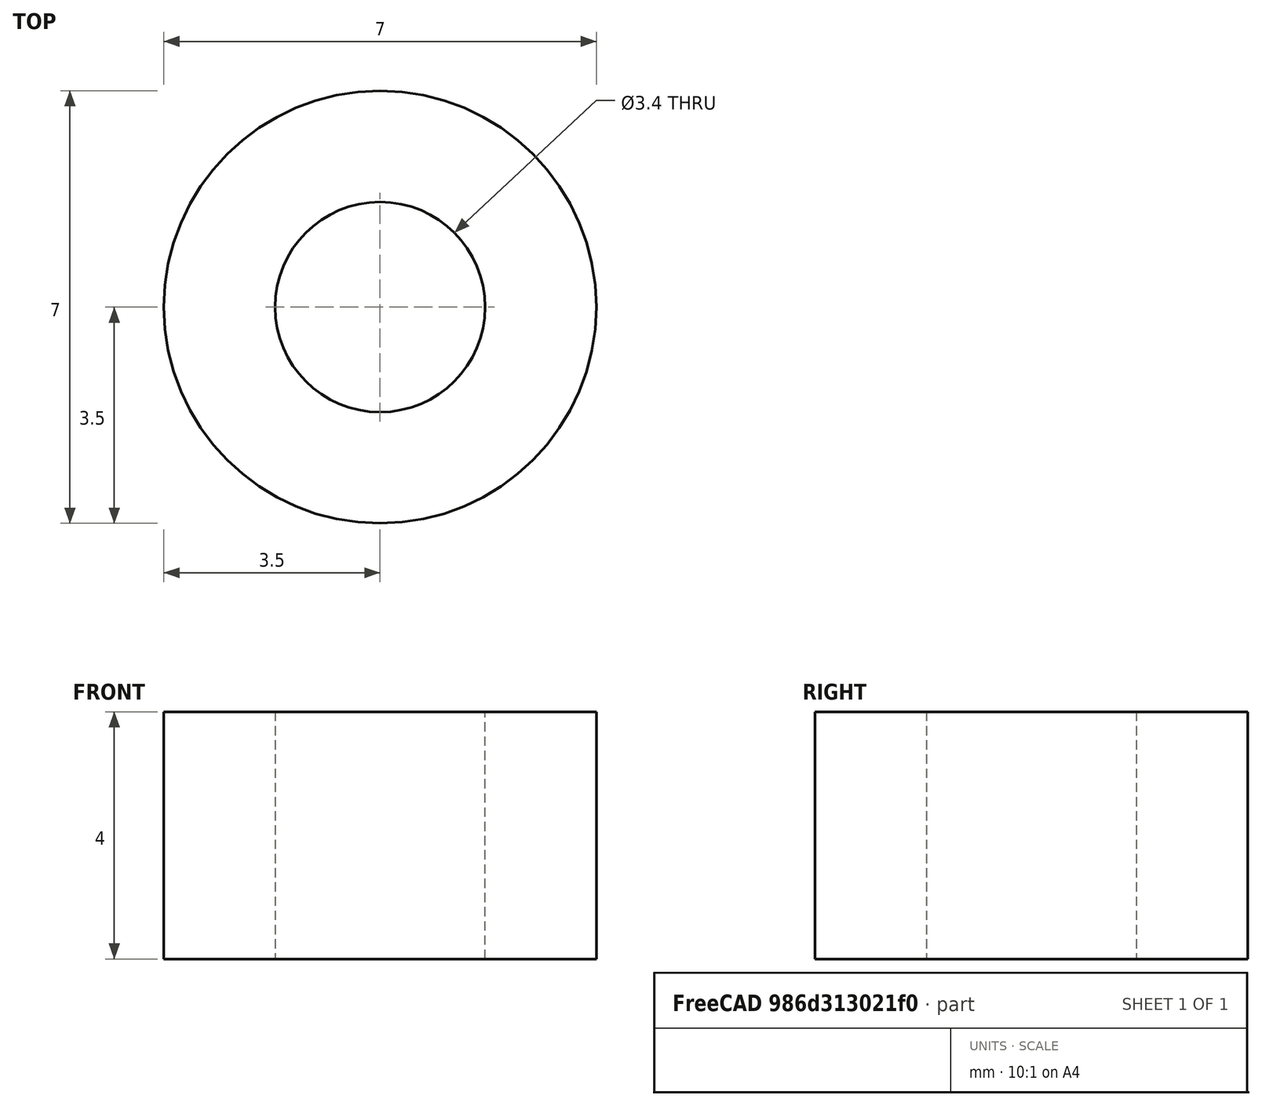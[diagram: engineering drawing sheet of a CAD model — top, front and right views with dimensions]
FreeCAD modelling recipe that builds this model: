
FCSTD DOCUMENT  (FreeCAD 0.19R23578 (Git))
Label: m3_spacer
License: All rights reserved
LicenseURL: http://en.wikipedia.org/wiki/All_rights_reserved
objects: Sketcher::SketchObject×1, PartDesign::Pad×1, PartDesign::Body×1, Mesh::Feature×1
note: 4 computed .brp shape members not serialized (recipe doc carries the construction recipe); baked Part::Feature solids carry a one-line shape summary decoded from their .brp

FEATURE [Sketcher::SketchObject] Sketch
  MapMode = 5
  Support = -> [XY_Plane]
  sketch-geometry (2):
    g0: Circle CenterX=0 CenterY=0 CenterZ=0 NormalX=0 NormalY=0 NormalZ=1 AngleXU=0 Radius=1.7
    g1: Circle CenterX=0 CenterY=0 CenterZ=0 NormalX=0 NormalY=0 NormalZ=1 AngleXU=0 Radius=3.5
  constraints (4):
    c: Coincident(g0,g-1)
    c: Coincident(g1,g0)
    c: Diameter(g0) = 3.4
    c: Diameter(g1) = 7
FEATURE [PartDesign::Pad] Pad
  Direction = (1,1,1)
  Length = 4
  Length2 = 100
  Profile = -> Sketch
  Type = 0
FEATURE [PartDesign::Body] Body
  Group = -> [Sketch,Pad]
  Origin = -> Origin
  Tip = -> Pad
FEATURE [Mesh::Feature] Mesh  label="Pad (Meshed)"
